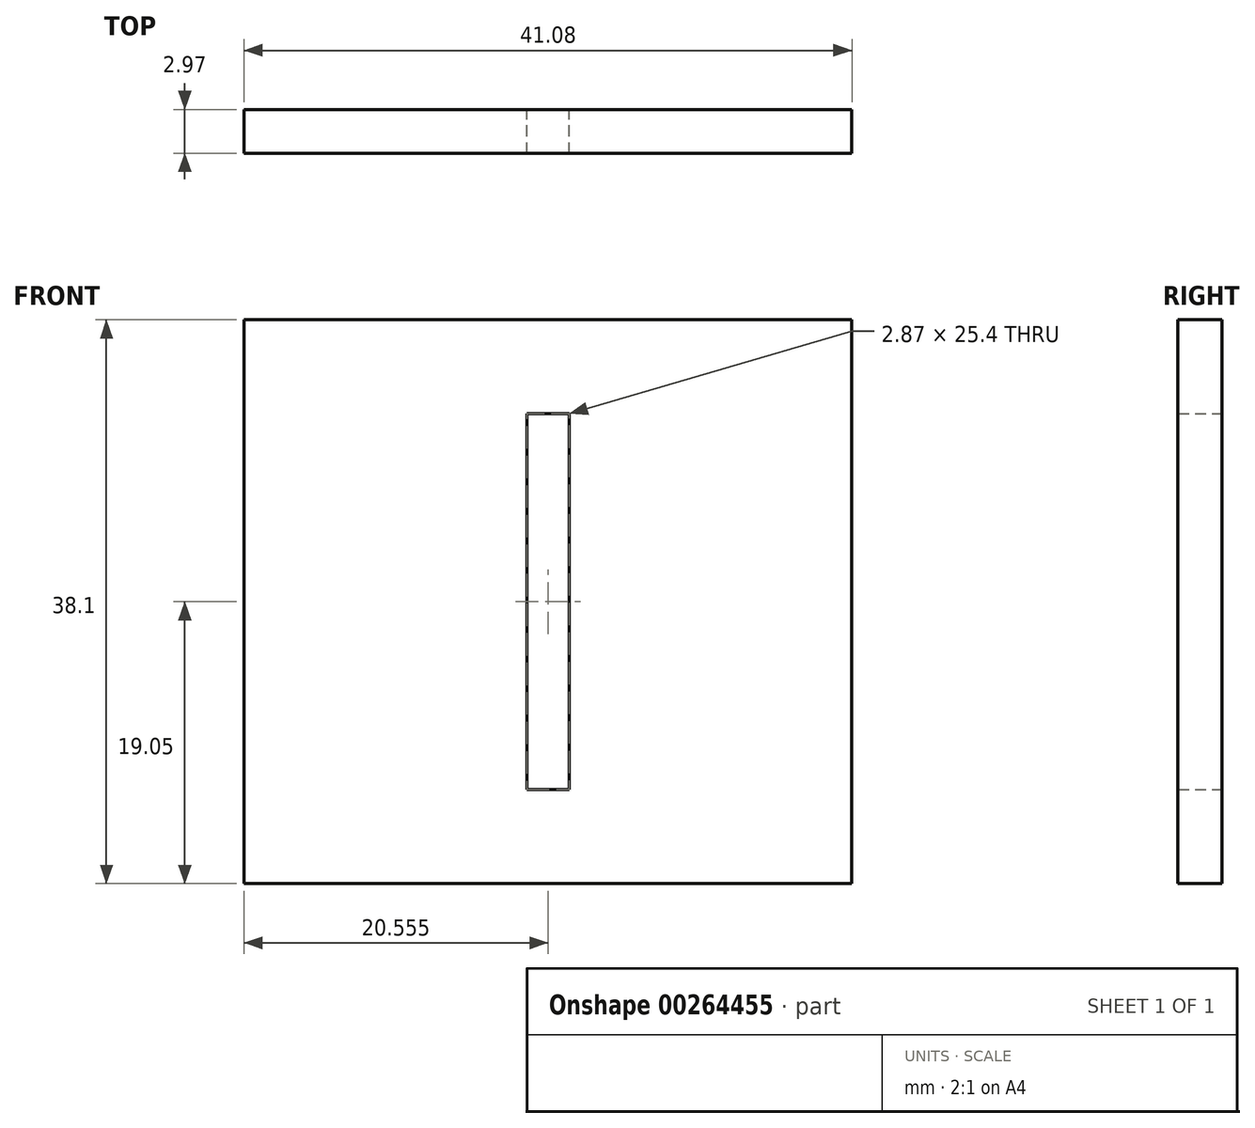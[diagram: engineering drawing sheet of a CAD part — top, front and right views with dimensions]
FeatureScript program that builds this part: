
annotation { "Feature Type Name" : "Feature", "Feature Type Description" : "" }
export const myFeature = defineFeature(function(context is Context, id is Id, definition is map)
    precondition{}
    {
        {
            var Q0;
            Q0=qCreatedBy(makeId("Front.planeOp"),FACE);
            var sketch = newSketch(context, id + "F0", { "sketchPlane" : qUnion([Q0])});
            skLineSegment(sketch, "E0", {"start": v(20.54, 0) * mm, "end": v(20.54, -38.1) * mm});
            skLineSegment(sketch, "E1.MirrorCS", {"start": v(-20.54, 0) * mm, "end": v(-20.54, -38.1) * mm});
            skLineSegment(sketch, "E2", {"start": v(-20.54, 0) * mm, "end": v(20.54, 0) * mm});
            skLineSegment(sketch, "E3", {"start": v(-20.54, -38.1) * mm, "end": v(20.54, -38.1) * mm});
            skLineSegment(sketch, "E4", {"start": v(-1.42, -6.35) * mm, "end": v(1.45, -6.35) * mm});
            skLineSegment(sketch, "E5", {"start": v(-1.42, -6.35) * mm, "end": v(-1.42, -31.75) * mm});
            skLineSegment(sketch, "E6", {"start": v(-1.42, -31.75) * mm, "end": v(1.45, -31.75) * mm});
            skLineSegment(sketch, "E7", {"start": v(1.45, -31.75) * mm, "end": v(1.45, -6.35) * mm});
            skSolve(sketch);
        }
        {
            var Q0;
            Q0=makeQuery(id+"F0.imprint","IMPRINT",FACE,{"disambiguationData":[TD([[makeQuery(id+"F0.imprint","IMPRINT",EDGE,{"derivedFrom":sQuery(id+"F0.wireOp",EDGE,"E0")}),-1.0]])]});
            extrude(context, id + "F1", {"entities" : qUnion([Q0]), "depth" : 2.97 * mm});
        }
    });
